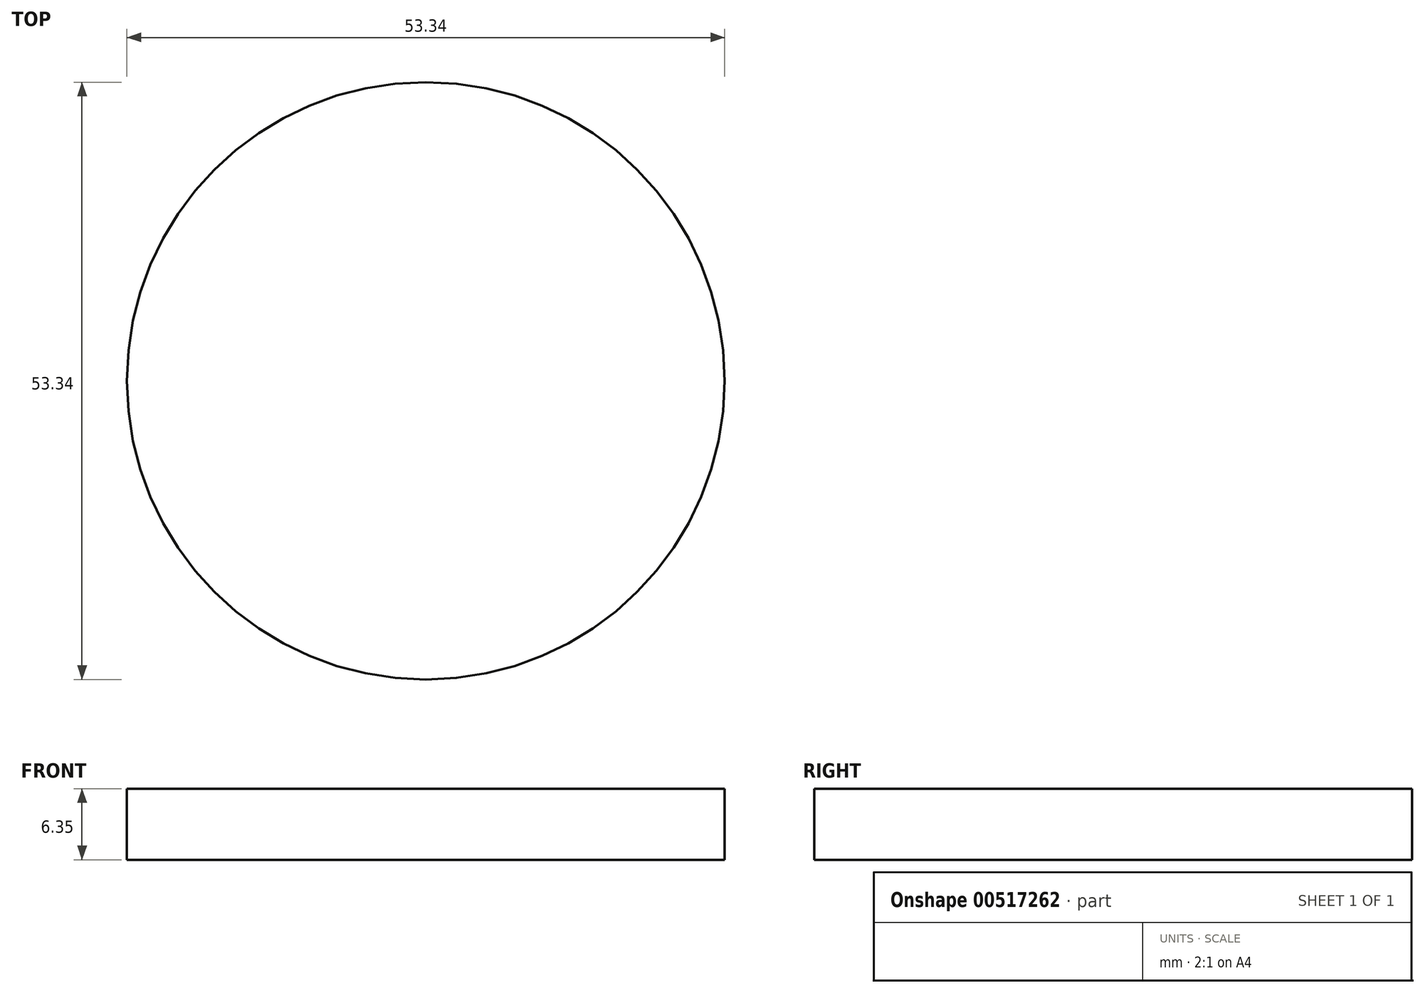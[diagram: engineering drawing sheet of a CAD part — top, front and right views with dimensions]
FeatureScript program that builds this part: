
annotation { "Feature Type Name" : "Feature", "Feature Type Description" : "" }
export const myFeature = defineFeature(function(context is Context, id is Id, definition is map)
    precondition{}
    {
        {
            var Q0;
            Q0=qCreatedBy(makeId("Top.planeOp"),FACE);
            var sketch = newSketch(context, id + "F0", { "sketchPlane" : qUnion([Q0])});
            skCircle(sketch, "E0", {"center": v(0, 0) * mm, "radius": 26.67 * mm});
            skSolve(sketch);
        }
        {
            var Q0;
            Q0 = qSketchRegion(id + "F0", true);
            extrude(context, id + "F1", {"entities" : qUnion([Q0]), "depth" : 6.35 * mm, "offsetDistance" : 25.4 * mm});
        }
    });
